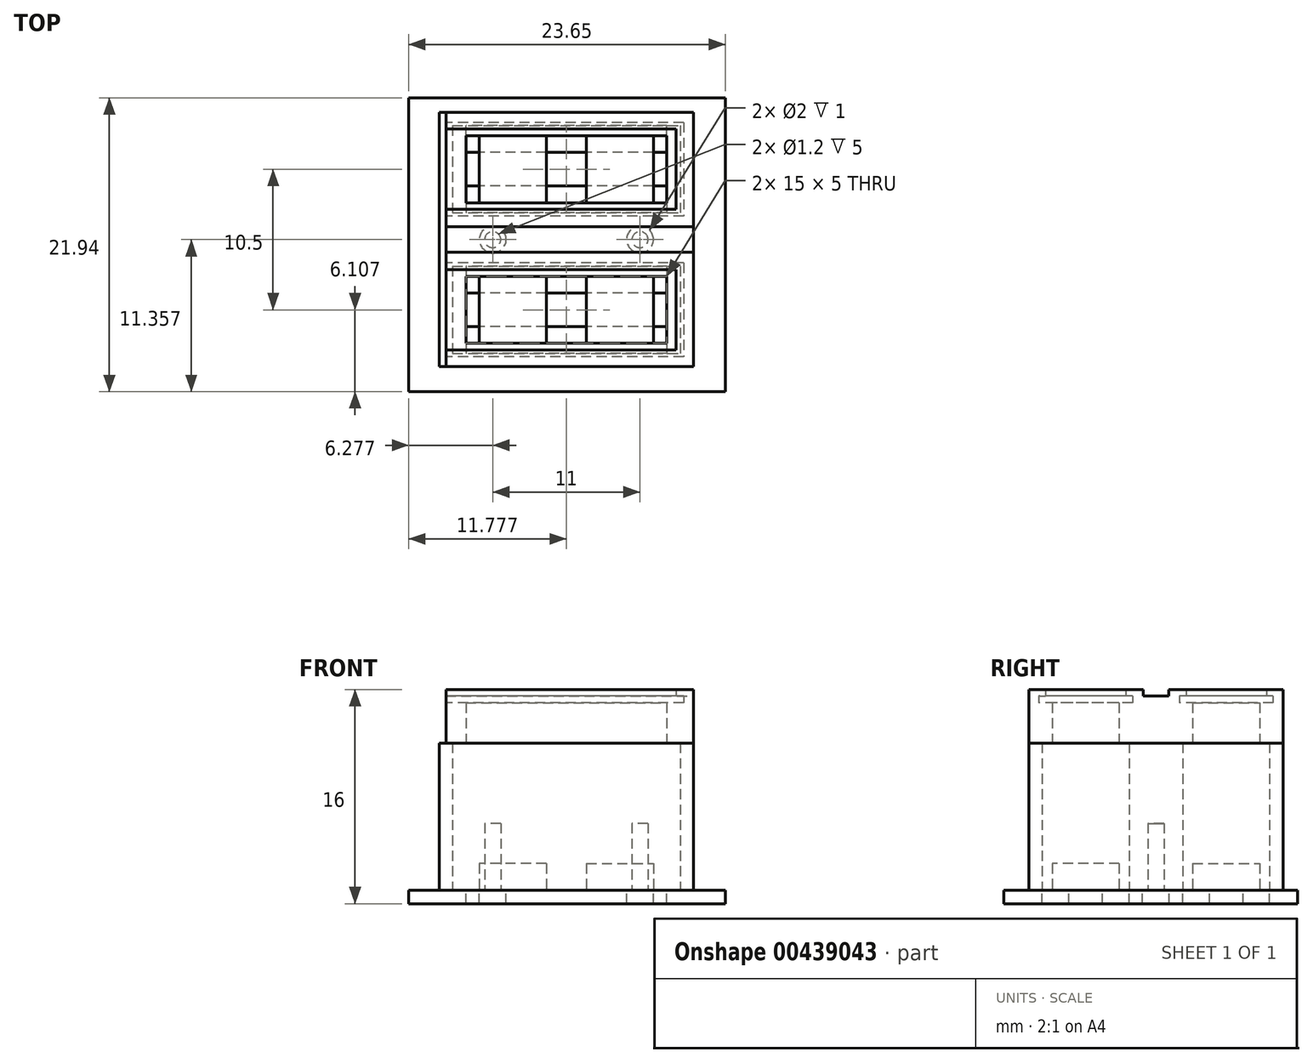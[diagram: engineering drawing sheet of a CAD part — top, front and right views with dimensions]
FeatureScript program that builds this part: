
annotation { "Feature Type Name" : "Feature", "Feature Type Description" : "" }
export const myFeature = defineFeature(function(context is Context, id is Id, definition is map)
    precondition{}
    {
        {
            var Q0;
            Q0=qCreatedBy(makeId("Top.planeOp"),FACE);
            var sketch = newSketch(context, id + "F0", { "sketchPlane" : qUnion([Q0])});
            skLineSegment(sketch, "E0.bottom", {"start": v(17.66, 9.32) * mm, "end": v(36.66, 9.32) * mm});
            skLineSegment(sketch, "E0.top", {"start": v(17.66, -9.68) * mm, "end": v(36.66, -9.68) * mm});
            skLineSegment(sketch, "E0.left", {"start": v(17.66, 9.32) * mm, "end": v(17.66, -9.68) * mm});
            skLineSegment(sketch, "E0.right", {"start": v(36.66, 9.32) * mm, "end": v(36.66, -9.68) * mm});
            skLineSegment(sketch, "E1.bottom", {"start": v(18.66, 8.32) * mm, "end": v(35.66, 8.32) * mm});
            skLineSegment(sketch, "E1.top", {"start": v(18.66, 1.82) * mm, "end": v(35.66, 1.82) * mm});
            skLineSegment(sketch, "E1.left", {"start": v(18.66, 8.32) * mm, "end": v(18.66, 1.82) * mm});
            skLineSegment(sketch, "E1.right", {"start": v(35.66, 8.32) * mm, "end": v(35.66, 1.82) * mm});
            skLineSegment(sketch, "E2.bottom", {"start": v(18.66, -2.18) * mm, "end": v(35.66, -2.18) * mm});
            skLineSegment(sketch, "E2.top", {"start": v(18.66, -8.68) * mm, "end": v(35.66, -8.68) * mm});
            skLineSegment(sketch, "E2.left", {"start": v(18.66, -2.18) * mm, "end": v(18.66, -8.68) * mm});
            skLineSegment(sketch, "E2.right", {"start": v(35.66, -2.18) * mm, "end": v(35.66, -8.68) * mm});
            skCircle(sketch, "E3", {"center": v(21.66, -0.18) * mm, "radius": 0.6 * mm, "construction": true});
            skCircle(sketch, "E4", {"center": v(32.66, -0.18) * mm, "radius": 0.6 * mm, "construction": true});
            skSolve(sketch);
        }
        {
            var Q0;
            Q0=qSketchRegion(id+"F0",true);
            extrude(context, id + "F1", {"entities" : qUnion([Q0]), "depth" : 11 * mm});
        }
        {
            var Q0;
            Q0=qCreatedBy(makeId("Top.planeOp"),FACE);
            var sketch = newSketch(context, id + "F2", { "sketchPlane" : qUnion([Q0])});
            skLineSegment(sketch, "E5.bottom", {"start": v(25.66, 2.57) * mm, "end": v(20.66, 2.57) * mm});
            skLineSegment(sketch, "E5.top", {"start": v(25.66, 7.57) * mm, "end": v(20.66, 7.57) * mm});
            skLineSegment(sketch, "E5.left", {"start": v(25.66, 2.57) * mm, "end": v(25.66, 7.57) * mm});
            skLineSegment(sketch, "E5.right", {"start": v(20.66, 2.57) * mm, "end": v(20.66, 7.57) * mm});
            skPoint(sketch, "E5.middle", {"position": v(23.16, 5.07) * mm});
            skLineSegment(sketch, "E6.bottom", {"start": v(25.66, -2.93) * mm, "end": v(20.66, -2.93) * mm});
            skLineSegment(sketch, "E6.top", {"start": v(25.66, -7.93) * mm, "end": v(20.66, -7.93) * mm});
            skLineSegment(sketch, "E6.left", {"start": v(25.66, -2.93) * mm, "end": v(25.66, -7.93) * mm});
            skLineSegment(sketch, "E6.right", {"start": v(20.66, -2.93) * mm, "end": v(20.66, -7.93) * mm});
            skPoint(sketch, "E6.middle", {"position": v(23.16, -5.43) * mm});
            skLineSegment(sketch, "E7.bottom", {"start": v(28.66, 2.57) * mm, "end": v(33.66, 2.57) * mm});
            skLineSegment(sketch, "E7.top", {"start": v(28.66, 7.57) * mm, "end": v(33.66, 7.57) * mm});
            skLineSegment(sketch, "E7.left", {"start": v(28.66, 2.57) * mm, "end": v(28.66, 7.57) * mm});
            skLineSegment(sketch, "E7.right", {"start": v(33.66, 2.57) * mm, "end": v(33.66, 7.57) * mm});
            skPoint(sketch, "E7.middle", {"position": v(31.16, 5.07) * mm});
            skLineSegment(sketch, "E8.bottom", {"start": v(28.66, -7.93) * mm, "end": v(33.66, -7.93) * mm});
            skLineSegment(sketch, "E8.top", {"start": v(28.66, -2.93) * mm, "end": v(33.66, -2.93) * mm});
            skLineSegment(sketch, "E8.left", {"start": v(28.66, -7.93) * mm, "end": v(28.66, -2.93) * mm});
            skLineSegment(sketch, "E8.right", {"start": v(33.66, -7.93) * mm, "end": v(33.66, -2.93) * mm});
            skPoint(sketch, "E8.middle", {"position": v(31.16, -5.43) * mm});
            skSolve(sketch);
        }
        {
            var Q0;
            Q0=qSketchRegion(id+"F2",true);
            extrude(context, id + "F3", {"entities" : qUnion([Q0]), "depth" : 2 * mm});
        }
        {
            var Q0;
            Q0=makeQuery(id+"F1.opExtrude","CAP_FACE",FACE,{"disambiguationData":[OSD([sQuery(id+"F0.wireOp",EDGE,"E0.bottom"),sQuery(id+"F0.wireOp",EDGE,"E0.top"),sQuery(id+"F0.wireOp",EDGE,"E0.left"),sQuery(id+"F0.wireOp",EDGE,"E0.right"),sQuery(id+"F0.wireOp",EDGE,"E1.bottom"),sQuery(id+"F0.wireOp",EDGE,"E1.top"),sQuery(id+"F0.wireOp",EDGE,"E1.left"),sQuery(id+"F0.wireOp",EDGE,"E1.right"),sQuery(id+"F0.wireOp",EDGE,"E2.bottom"),sQuery(id+"F0.wireOp",EDGE,"E2.top"),sQuery(id+"F0.wireOp",EDGE,"E2.left"),sQuery(id+"F0.wireOp",EDGE,"E2.right"),sQuery(id+"F0.wireOp",EDGE,"E3"),sQuery(id+"F0.wireOp",EDGE,"E4")])],"isStart":false});
            var sketch = newSketch(context, id + "F4", { "sketchPlane" : qUnion([Q0])});
            skLineSegment(sketch, "E9.bottom", {"start": v(18.16, 9.32) * mm, "end": v(36.66, 9.32) * mm});
            skLineSegment(sketch, "E9.top", {"start": v(18.16, -9.68) * mm, "end": v(36.66, -9.68) * mm});
            skLineSegment(sketch, "E9.left", {"start": v(18.16, 9.32) * mm, "end": v(18.16, -9.68) * mm});
            skLineSegment(sketch, "E9.right", {"start": v(36.66, 9.32) * mm, "end": v(36.66, -9.68) * mm});
            skLineSegment(sketch, "E10.bottom", {"start": v(19.66, -2.93) * mm, "end": v(34.66, -2.93) * mm});
            skLineSegment(sketch, "E10.top", {"start": v(19.66, -7.93) * mm, "end": v(34.66, -7.93) * mm});
            skLineSegment(sketch, "E10.left", {"start": v(19.66, -2.93) * mm, "end": v(19.66, -7.93) * mm});
            skLineSegment(sketch, "E10.right", {"start": v(34.66, -2.93) * mm, "end": v(34.66, -7.93) * mm});
            skLineSegment(sketch, "E11.bottom", {"start": v(19.66, 2.57) * mm, "end": v(34.66, 2.57) * mm});
            skLineSegment(sketch, "E11.top", {"start": v(19.66, 7.57) * mm, "end": v(34.66, 7.57) * mm});
            skLineSegment(sketch, "E11.left", {"start": v(19.66, 2.57) * mm, "end": v(19.66, 7.57) * mm});
            skLineSegment(sketch, "E11.right", {"start": v(34.66, 2.57) * mm, "end": v(34.66, 7.57) * mm});
            skSolve(sketch);
        }
        {
            var Q0;
            Q0=qSketchRegion(id+"F4",true);
            extrude(context, id + "F5", {"entities" : qUnion([Q0]), "depth" : 3 * mm});
        }
        {
            var Q0;
            Q0=makeQuery(id+"F5.opExtrude","CAP_FACE",FACE,{"disambiguationData":[OSD([sQuery(id+"F4.wireOp",EDGE,"E9.bottom"),sQuery(id+"F4.wireOp",EDGE,"E9.top"),sQuery(id+"F4.wireOp",EDGE,"E9.left"),sQuery(id+"F4.wireOp",EDGE,"E9.right"),sQuery(id+"F4.wireOp",EDGE,"E10.bottom"),sQuery(id+"F4.wireOp",EDGE,"E10.top"),sQuery(id+"F4.wireOp",EDGE,"E10.left"),sQuery(id+"F4.wireOp",EDGE,"E10.right"),sQuery(id+"F4.wireOp",EDGE,"E11.bottom"),sQuery(id+"F4.wireOp",EDGE,"E11.top"),sQuery(id+"F4.wireOp",EDGE,"E11.left"),sQuery(id+"F4.wireOp",EDGE,"E11.right")])],"isStart":false});
            var sketch = newSketch(context, id + "F6", { "sketchPlane" : qUnion([Q0])});
            skLineSegment(sketch, "E12.bottom", {"start": v(36.66, 9.32) * mm, "end": v(35.9, 9.32) * mm});
            skLineSegment(sketch, "E12.top", {"start": v(36.66, -9.68) * mm, "end": v(35.9, -9.68) * mm});
            skLineSegment(sketch, "E12.left", {"start": v(36.66, 9.32) * mm, "end": v(36.66, -9.68) * mm});
            skLineSegment(sketch, "E12.right", {"start": v(35.9, 9.32) * mm, "end": v(35.9, -9.68) * mm});
            skLineSegment(sketch, "E13.bottom", {"start": v(35.9, 9.32) * mm, "end": v(18.16, 9.32) * mm});
            skLineSegment(sketch, "E13.top", {"start": v(35.9, 8.57) * mm, "end": v(18.16, 8.57) * mm});
            skLineSegment(sketch, "E13.left", {"start": v(35.9, 9.32) * mm, "end": v(35.9, 8.57) * mm});
            skLineSegment(sketch, "E13.right", {"start": v(18.16, 9.32) * mm, "end": v(18.16, 8.57) * mm});
            skLineSegment(sketch, "E14.bottom", {"start": v(35.9, -9.68) * mm, "end": v(18.16, -9.68) * mm});
            skLineSegment(sketch, "E14.top", {"start": v(35.9, -8.93) * mm, "end": v(18.16, -8.93) * mm});
            skLineSegment(sketch, "E14.left", {"start": v(35.9, -9.68) * mm, "end": v(35.9, -8.93) * mm});
            skLineSegment(sketch, "E14.right", {"start": v(18.16, -9.68) * mm, "end": v(18.16, -8.93) * mm});
            skLineSegment(sketch, "E15.bottom", {"start": v(35.9, 1.57) * mm, "end": v(18.16, 1.57) * mm});
            skLineSegment(sketch, "E15.top", {"start": v(35.9, -1.93) * mm, "end": v(18.16, -1.93) * mm});
            skLineSegment(sketch, "E15.left", {"start": v(35.9, 1.57) * mm, "end": v(35.9, -1.93) * mm});
            skLineSegment(sketch, "E15.right", {"start": v(18.16, 1.57) * mm, "end": v(18.16, -1.93) * mm});
            skSolve(sketch);
        }
        {
            var Q0;
            Q0=qSketchRegion(id+"F6",true);
            extrude(context, id + "F7", {"entities" : qUnion([Q0]), "operationType" : NewBodyOperationType.ADD, "depth" : 0.5 * mm});
        }
        {
            var Q0;
            Q0=makeQuery(id+"F7.opExtrude","CAP_FACE",FACE,{"disambiguationData":[OSD([sQuery(id+"F6.wireOp",EDGE,"E12.bottom"),sQuery(id+"F6.wireOp",EDGE,"E12.top"),sQuery(id+"F6.wireOp",EDGE,"E12.left"),sQuery(id+"F6.wireOp",EDGE,"E12.right"),sQuery(id+"F6.wireOp",EDGE,"E13.bottom"),sQuery(id+"F6.wireOp",EDGE,"E13.top"),sQuery(id+"F6.wireOp",EDGE,"E13.right"),sQuery(id+"F6.wireOp",EDGE,"E14.bottom"),sQuery(id+"F6.wireOp",EDGE,"E14.top"),sQuery(id+"F6.wireOp",EDGE,"E14.right"),sQuery(id+"F6.wireOp",EDGE,"E15.bottom"),sQuery(id+"F6.wireOp",EDGE,"E15.top"),sQuery(id+"F6.wireOp",EDGE,"E15.right")])],"isStart":false});
            var sketch = newSketch(context, id + "F8", { "sketchPlane" : qUnion([Q0])});
            skLineSegment(sketch, "E16.bottom", {"start": v(36.66, 9.32) * mm, "end": v(35.36, 9.32) * mm});
            skLineSegment(sketch, "E16.top", {"start": v(36.66, -9.68) * mm, "end": v(35.36, -9.68) * mm});
            skLineSegment(sketch, "E16.left", {"start": v(36.66, 9.32) * mm, "end": v(36.66, -9.68) * mm});
            skLineSegment(sketch, "E16.right", {"start": v(35.36, 9.32) * mm, "end": v(35.36, -9.68) * mm});
            skLineSegment(sketch, "E17.bottom", {"start": v(18.16, 9.32) * mm, "end": v(35.36, 9.32) * mm});
            skLineSegment(sketch, "E17.top", {"start": v(18.16, 8.07) * mm, "end": v(35.36, 8.07) * mm});
            skLineSegment(sketch, "E17.left", {"start": v(18.16, 9.32) * mm, "end": v(18.16, 8.07) * mm});
            skLineSegment(sketch, "E17.right", {"start": v(35.36, 9.32) * mm, "end": v(35.36, 8.07) * mm});
            skLineSegment(sketch, "E18.bottom", {"start": v(18.16, -9.68) * mm, "end": v(35.36, -9.68) * mm});
            skLineSegment(sketch, "E18.top", {"start": v(18.16, -8.43) * mm, "end": v(35.36, -8.43) * mm});
            skLineSegment(sketch, "E18.left", {"start": v(18.16, -9.68) * mm, "end": v(18.16, -8.43) * mm});
            skLineSegment(sketch, "E18.right", {"start": v(35.36, -9.68) * mm, "end": v(35.36, -8.43) * mm});
            skLineSegment(sketch, "E19.bottom", {"start": v(35.36, 2.07) * mm, "end": v(18.16, 2.07) * mm});
            skLineSegment(sketch, "E19.top", {"start": v(35.36, -2.43) * mm, "end": v(18.16, -2.43) * mm});
            skLineSegment(sketch, "E19.left", {"start": v(35.36, 2.07) * mm, "end": v(35.36, -2.43) * mm});
            skLineSegment(sketch, "E19.right", {"start": v(18.16, 2.07) * mm, "end": v(18.16, -2.43) * mm});
            skSolve(sketch);
        }
        {
            var Q0;
            Q0=qSketchRegion(id+"F8",true);
            extrude(context, id + "F9", {"entities" : qUnion([Q0]), "operationType" : NewBodyOperationType.ADD, "depth" : 0.5 * mm});
        }
        {
            var Q0;
            Q0=makeQuery(id+"F9.opExtrude","CAP_FACE",FACE,{"disambiguationData":[OSD([sQuery(id+"F8.wireOp",EDGE,"E16.bottom"),sQuery(id+"F8.wireOp",EDGE,"E16.top"),sQuery(id+"F8.wireOp",EDGE,"E16.left"),sQuery(id+"F8.wireOp",EDGE,"E16.right"),sQuery(id+"F8.wireOp",EDGE,"E17.bottom"),sQuery(id+"F8.wireOp",EDGE,"E17.top"),sQuery(id+"F8.wireOp",EDGE,"E17.left"),sQuery(id+"F8.wireOp",EDGE,"E18.bottom"),sQuery(id+"F8.wireOp",EDGE,"E18.top"),sQuery(id+"F8.wireOp",EDGE,"E18.left"),sQuery(id+"F8.wireOp",EDGE,"E19.bottom"),sQuery(id+"F8.wireOp",EDGE,"E19.top"),sQuery(id+"F8.wireOp",EDGE,"E19.right")])],"isStart":false});
            var sketch = newSketch(context, id + "F10", { "sketchPlane" : qUnion([Q0])});
            skLineSegment(sketch, "E20.bottom", {"start": v(18.16, 0.77) * mm, "end": v(36.66, 0.77) * mm});
            skLineSegment(sketch, "E20.top", {"start": v(18.16, -1.13) * mm, "end": v(36.66, -1.13) * mm});
            skLineSegment(sketch, "E20.left", {"start": v(18.16, 0.77) * mm, "end": v(18.16, -1.13) * mm});
            skLineSegment(sketch, "E20.right", {"start": v(36.66, 0.77) * mm, "end": v(36.66, -1.13) * mm});
            skSolve(sketch);
        }
        {
            var Q0;
            Q0=qSketchRegion(id+"F10",true);
            extrude(context, id + "F11", {"entities" : qUnion([Q0]), "operationType" : NewBodyOperationType.REMOVE, "oppositeDirection" : true, "depth" : 0.5 * mm});
        }
        {
            var Q0;
            Q0=qCreatedBy(makeId("Top.planeOp"),FACE);
            var sketch = newSketch(context, id + "F12", { "sketchPlane" : qUnion([Q0])});
            skLineSegment(sketch, "E21.bottom", {"start": v(15.38, 10.4) * mm, "end": v(39.03, 10.4) * mm});
            skLineSegment(sketch, "E21.top", {"start": v(15.38, -11.54) * mm, "end": v(39.03, -11.54) * mm});
            skLineSegment(sketch, "E21.left", {"start": v(15.38, 10.4) * mm, "end": v(15.38, -11.54) * mm});
            skLineSegment(sketch, "E21.right", {"start": v(39.03, 10.4) * mm, "end": v(39.03, -11.54) * mm});
            skCircle(sketch, "E22", {"center": v(21.66, -0.18) * mm, "radius": 1 * mm});
            skCircle(sketch, "E23", {"center": v(32.66, -0.18) * mm, "radius": 1 * mm});
            skPoint(sketch, "E24", {"position": v(27.16, -0.18) * mm});
            skLineSegment(sketch, "E25.bottom", {"start": v(34.66, 6.32) * mm, "end": v(19.66, 6.32) * mm});
            skLineSegment(sketch, "E25.top", {"start": v(34.66, 8.32) * mm, "end": v(19.66, 8.32) * mm});
            skLineSegment(sketch, "E25.left", {"start": v(34.66, 6.32) * mm, "end": v(34.66, 8.32) * mm});
            skLineSegment(sketch, "E25.right", {"start": v(19.66, 6.32) * mm, "end": v(19.66, 8.32) * mm});
            skPoint(sketch, "E25.middle", {"position": v(27.16, 7.32) * mm});
            skLineSegment(sketch, "E26.bottom", {"start": v(34.66, 3.82) * mm, "end": v(19.66, 3.82) * mm});
            skLineSegment(sketch, "E26.top", {"start": v(34.66, 1.82) * mm, "end": v(19.66, 1.82) * mm});
            skLineSegment(sketch, "E26.left", {"start": v(34.66, 3.82) * mm, "end": v(34.66, 1.82) * mm});
            skLineSegment(sketch, "E26.right", {"start": v(19.66, 3.82) * mm, "end": v(19.66, 1.82) * mm});
            skPoint(sketch, "E26.middle", {"position": v(27.16, 2.82) * mm});
            skLineSegment(sketch, "E27.bottom", {"start": v(34.66, -2.18) * mm, "end": v(19.66, -2.18) * mm});
            skLineSegment(sketch, "E27.top", {"start": v(34.66, -4.18) * mm, "end": v(19.66, -4.18) * mm});
            skLineSegment(sketch, "E27.left", {"start": v(34.66, -2.18) * mm, "end": v(34.66, -4.18) * mm});
            skLineSegment(sketch, "E27.right", {"start": v(19.66, -2.18) * mm, "end": v(19.66, -4.18) * mm});
            skPoint(sketch, "E27.middle", {"position": v(27.16, -3.18) * mm});
            skLineSegment(sketch, "E28.bottom", {"start": v(34.66, -6.68) * mm, "end": v(19.66, -6.68) * mm});
            skLineSegment(sketch, "E28.top", {"start": v(34.66, -8.68) * mm, "end": v(19.66, -8.68) * mm});
            skLineSegment(sketch, "E28.left", {"start": v(34.66, -6.68) * mm, "end": v(34.66, -8.68) * mm});
            skLineSegment(sketch, "E28.right", {"start": v(19.66, -6.68) * mm, "end": v(19.66, -8.68) * mm});
            skPoint(sketch, "E28.middle", {"position": v(27.16, -7.68) * mm});
            skSolve(sketch);
        }
        {
            var Q0;
            Q0=qSketchRegion(id+"F12",true);
            extrude(context, id + "F13", {"entities" : qUnion([Q0]), "oppositeDirection" : true, "depth" : 1 * mm});
        }
        {
            var Q0;
            Q0=makeQuery(id+"F13.opExtrude","CAP_FACE",FACE,{"disambiguationData":[OSD([sQuery(id+"F12.wireOp",EDGE,"E21.bottom"),sQuery(id+"F12.wireOp",EDGE,"E21.top"),sQuery(id+"F12.wireOp",EDGE,"E21.left"),sQuery(id+"F12.wireOp",EDGE,"E21.right")])],"isStart":true});
            var sketch = newSketch(context, id + "F14", { "sketchPlane" : qUnion([Q0])});
            skLineSegment(sketch, "E29.bottom", {"start": v(29.1, -2.18) * mm, "end": v(25.2, -2.18) * mm});
            skLineSegment(sketch, "E29.top", {"start": v(29.1, 1.82) * mm, "end": v(25.2, 1.82) * mm});
            skLineSegment(sketch, "E29.left", {"start": v(29.1, -2.18) * mm, "end": v(29.1, 1.82) * mm});
            skLineSegment(sketch, "E29.right", {"start": v(25.2, -2.18) * mm, "end": v(25.2, 1.82) * mm});
            skPoint(sketch, "E29.middle", {"position": v(27.16, -0.18) * mm});
            skSolve(sketch);
        }
        {
            var Q0;
            Q0=qSketchRegion(id+"F14",true);
            extrude(context, id + "F15", {"entities" : qUnion([Q0]), "operationType" : NewBodyOperationType.ADD, "depth" : 2.9 * mm});
        }
        {
            var Q0;
            Q0=makeQuery(id+"F0.imprint","IMPRINT",FACE,{"disambiguationData":[TD([[makeQuery(id+"F0.imprint","IMPRINT",EDGE,{"derivedFrom":sQuery(id+"F0.wireOp",EDGE,"E0.bottom")}),-1.0]])]});
            var sketch = newSketch(context, id + "F16", { "sketchPlane" : qUnion([Q0])});
            skCircle(sketch, "E30", {"center": v(21.66, -0.18) * mm, "radius": 0.6 * mm});
            skCircle(sketch, "E31", {"center": v(32.66, -0.18) * mm, "radius": 0.6 * mm});
            skSolve(sketch);
        }
        {
            var Q0;
            Q0=qSketchRegion(id+"F16",true);
            extrude(context, id + "F17", {"entities" : qUnion([Q0]), "operationType" : NewBodyOperationType.REMOVE, "depth" : 5 * mm});
        }
    });
